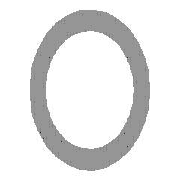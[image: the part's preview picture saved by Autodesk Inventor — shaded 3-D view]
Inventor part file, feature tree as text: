
AUTODESK INVENTOR PART (.ipt)
format: ipt  version: 2025 (Build 290162010, 162A)  size: 122,880 bytes
history: native  units: mm (DEFAULTED — no unit token found)
features: other x3, sketch x1, plane x1
ambient origin geometry x8: Origin, YZ Plane, XZ Plane, XY Plane, X Axis, Y Axis, Z Axis, Center Point
bodies: Solid1 (feature_tree), Body (feature_tree)
feature tree (5):
  other  "Driven Length"
  other  "Start plane"
  other  "End plane"
  sketch  "Sketch3"  dims[d0=168.3mm d1=2.0mm d2=200.0mm d3=0.0mm d4=-0.0mm d5=200.0mm d6=90.0deg d7=200.0mm]
  plane  "Work Plane3"
